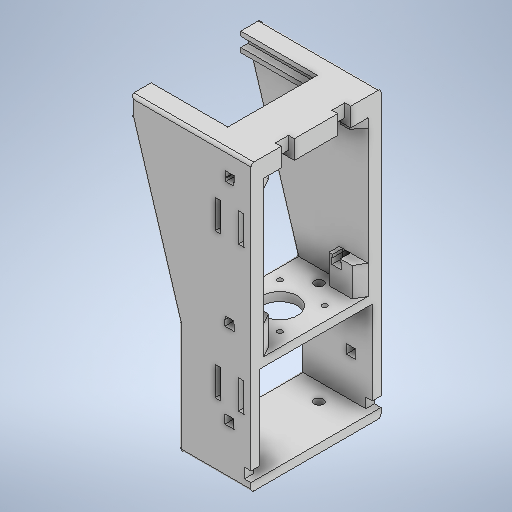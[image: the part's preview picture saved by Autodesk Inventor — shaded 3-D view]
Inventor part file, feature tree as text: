
AUTODESK INVENTOR PART (.ipt)
format: ipt  version: 2025 (Build 290162000, 162)  size: 778,240 bytes
history: native  units: mm
features: extrude x31, sketch x31, fillet x1
ambient origin geometry x8: Origin, YZ Plane, XZ Plane, XY Plane, X Axis, Y Axis, Z Axis, Center Point
bodies: Volumenkörper1 (feature_tree)
feature tree (63):
  extrude  "Extrusion1"  Depth=83.0mm
  extrude  "Extrusion2"  Depth=77.0mm
  extrude  "Extrusion3"  Depth=90.0mm TaperAngle=0.0deg
  extrude  "Extrusion4"  Depth=9.0mm
  extrude  "Extrusion5"  Depth=6.0mm
  extrude  "Extrusion6"  Depth=6.0mm
  extrude  "Extrusion7"  Depth=14.0mm
  extrude  "Extrusion8"  Depth=14.0mm
  extrude  "Extrusion9"  Depth=30.0mm
  extrude  "Extrusion10"  Depth=30.0mm
  extrude  "Extrusion11"  Depth=4.05mm
  extrude  "Extrusion12"  Depth=13.0mm
  extrude  "Extrusion13"  Depth=3.15mm
  extrude  "Extrusion14"  Depth=3.15mm
  extrude  "Extrusion15"  Depth=4.025mm
  extrude  "Extrusion16"  Depth=9.0mm
  extrude  "Extrusion17"  Depth=9.075mm TaperAngle=0.0deg
  extrude  "Extrusion18"  Depth=6.0mm
  extrude  "Extrusion19"  Depth=9.0mm
  extrude  "Extrusion20"  Depth=9.075mm TaperAngle=0.0deg
  extrude  "Extrusion21"  Depth=6.26mm
  extrude  "Extrusion22"  Depth=18.0mm
  extrude  "Extrusion23"  Depth=25.0mm
  extrude  "Extrusion24"  Depth=45.0mm
  extrude  "Extrusion25"  Depth=24.0mm
  extrude  "Extrusion26"  Depth=6.0mm TaperAngle=0.0deg
  extrude  "Extrusion27"  Depth=1.0mm
  extrude  "Extrusion28"  Depth=10.0mm
  extrude  "Extrusion29"  Depth=1.5mm TaperAngle=0.0deg
  extrude  "Extrusion30"  Depth=4.0mm
  extrude  "Extrusion31"  Depth=2.0mm TaperAngle=0.0deg
  fillet  "Rundung1"  [1 undecoded]
  sketch  "Skizze1"  dims[d0=197.0mm d1=83.0mm]
  sketch  "Skizze2"  dims[d5=13.0mm d6=77.0mm]
  sketch  "Skizze3"  dims[d7=50.0mm d8=90.0mm d9=0.0mm]
  sketch  "Skizze4"  dims[d10=9.0mm d11=9.0mm]
  sketch  "Skizze5"  dims[d12=6.0mm d13=6.0mm]
  sketch  "Skizze6"  dims[d14=6.0mm d15=6.0mm]
  sketch  "Skizze7"  dims[d16=83.0mm d17=0.0mm d18=14.0mm]
  sketch  "Skizze8"  dims[d19=14.0mm d20=53.0mm]
  sketch  "Skizze9"  dims[d21=30.0mm d22=21.0mm]
  sketch  "Skizze10"  dims[d23=4.05mm d24=30.0mm]
  sketch  "Skizze11"  dims[d25=21.0mm d26=4.05mm]
  sketch  "Skizze12"  dims[d27=13.0mm d28=0.0mm d29=53.0mm]
  sketch  "Skizze13"  dims[d30=3.15mm d31=3.15mm]
  sketch  "Skizze14"  dims[d32=5.075mm d33=0.0mm d34=3.15mm]
  sketch  "Skizze15"  dims[d35=5.075mm d36=0.0mm d39=4.025mm]
  sketch  "Skizze16"  dims[d40=4.05mm d41=0.0mm d42=9.0mm]
  sketch  "Skizze17"  dims[d43=4.025mm d44=9.075mm d45=0.0mm]
  sketch  "Skizze18"  dims[d46=9.0mm d47=6.0mm]
  sketch  "Skizze19"  dims[d48=4.05mm d49=0.0mm d50=9.0mm]
  sketch  "Skizze20"  dims[d51=4.025mm d52=9.075mm d53=0.0mm]
  sketch  "Skizze21"  dims[d54=6.26mm d55=6.26mm]
  sketch  "Skizze22"  dims[d56=18.0mm d57=18.0mm]
  sketch  "Skizze23"  dims[d58=25.0mm d59=25.0mm]
  sketch  "Skizze24"  dims[d60=190.0mm d61=0.0mm d62=45.0mm]
  sketch  "Skizze25"  dims[d63=25.0mm d64=24.0mm]
  sketch  "Skizze26"  dims[d65=6.0mm d66=0.0mm d75=6.0mm d76=0.0mm]
  sketch  "Skizze27"  dims[d77=1.0mm d78=3.2mm]
  sketch  "Skizze28"  dims[d79=10.0mm d80=3.2mm]
  sketch  "Skizze29"  dims[d81=1.0mm d82=1.5mm d83=0.0mm]
  sketch  "Skizze30"  dims[d84=2.0mm d85=4.0mm]
  sketch  "Skizze31"  dims[d86=10.0mm d87=0.0mm d88=15.0mm d89=0.0mm d90=0.0mm d91=6.35mm d92=0.0mm d93=6.35mm d94=5.0mm d95=0.0mm d96=0.0mm d97=0.0mm d98=8.37mm d99=5.0mm d100=0.0mm d101=14.0mm d102=6.0mm d103=7.0mm d104=7.0mm d105=6.3mm d106=0.0mm d112=18.0mm d113=0.0mm d114=18.0mm d115=0.0mm d116=14.0mm d118=32.0mm d119=20.0mm d120=7.0mm d121=0.0mm d122=20.0mm d123=0.0mm d124=7.0mm d125=0.0mm d126=20.0mm d127=0.0mm d131=6.35mm d134=18.0mm d135=0.0mm d136=18.0mm d137=0.0mm d138=2.0mm d139=0.0mm d140=6.3mm d141=11.8mm d142=6.2mm d143=32.0mm d144=7.0mm d145=4.5mm d146=90.0mm d147=0.0mm d148=4.0mm d149=0.0mm d154=4.8mm d155=20.0mm d156=4.0mm d157=44.5mm d158=20.8mm d159=4.0mm d160=20.0mm d161=32.5mm d162=20.8mm d163=2.0mm d164=20.0mm d165=32.5mm d166=4.8mm d167=4.0mm d168=0.0mm d169=4.0mm d170=0.0mm d171=6.32mm d172=2.0mm d173=2.0mm d174=4.3mm d175=4.3mm d176=0.0mm d177=0.5mm d178=0.0mm d179=0.0mm d180=0.0mm d186=3.5mm d187=3.5mm d188=3.5mm d189=3.5mm d194=2.0mm d150=0.5mm d151=0.872665mm]
note: 1 required parameter value undecoded (feature->parameter linkage not recoverable at this tier; creation-order binding heuristic only, values carry confidence <= 0.55)
